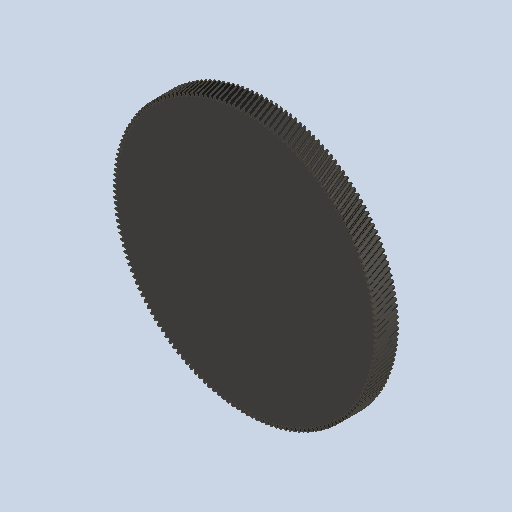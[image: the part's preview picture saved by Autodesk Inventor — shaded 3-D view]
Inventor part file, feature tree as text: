
AUTODESK INVENTOR PART (.ipt)
format: ipt  version: 2023 (Build 270158000, 158)  size: 1,941,504 bytes
history: native  units: mm (DEFAULTED — no unit token found)
features: plane x3, other x3, sketch x2, extrude x1
ambient origin geometry x8: Origin, YZ Plane, XZ Plane, XY Plane, X Axis, Y Axis, Z Axis, Center Point
bodies: Solid1 (feature_tree)
feature tree (9):
  extrude  "Extrusion1"  Depth=15.0mm TaperAngle=0.0deg
  plane  "Work Plane2"
  plane  "Work Plane8"
  plane  "Work Plane9"
  other  "Spur Gear"
  sketch  "Sketch1"  dims[d0=182.910221mm d1=15.0mm d2=0.0mm]
  sketch  "Sketch2"  dims[d3=180.910221mm d4=10.0mm d5=0.0mm d16=101.6mm d17=0.0mm d34=0.1848mm d39=0.0mm d41=0.0mm d43=101.6mm d46=101.6mm d47=0.0mm d48=0.0mm]
  other  "Srf1"
  other  "Pitch Diameter"
